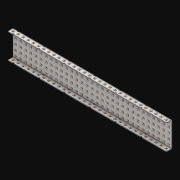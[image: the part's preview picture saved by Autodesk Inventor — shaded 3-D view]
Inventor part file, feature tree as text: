
AUTODESK INVENTOR PART (.ipt)
format: ipt  version: 2021 (Build 250183000, 183)  size: 3,827,200 bytes
history: native  units: in
note: dims shown in document units (in); Inventor stores cm internally (conversion verified against a paired STEP export)
features: extrude x218, other x217, sketch x4, thicken_offset x3, pattern_linear x3, imported_body x1
ambient origin geometry x8: Origin, YZ Plane, XZ Plane, XY Plane, X Axis, Y Axis, Z Axis, Center Point
bodies: Solid1 (feature_tree)
feature tree (446):
  thicken_offset  "Thicken1"
  thicken_offset  "Thicken2"
  thicken_offset  "Thicken3"
  pattern_linear  "Rectangular Pattern1"  Spacing1=0.001in  [1 undecoded]
  pattern_linear  "Rectangular Pattern2"  Spacing1=0.001in  [1 undecoded]
  pattern_linear  "Rectangular Pattern3"  Spacing1=0.182in  [1 undecoded]
  extrude  "Extrusion1"  Depth=0.063in TaperAngle=0.0deg
  sketch  "Sketch1"  dims[d0=0.001in]
  other  "Srf1"
  sketch  "Sketch2"  dims[d1=0.001in]
  other  "Srf2"
  sketch  "Sketch3"  dims[d2=0.001in]
  other  "Srf3"
  other  "Srf4"
  other  "Srf5"
  other  "Srf6"
  other  "Srf7"
  other  "Srf8"
  other  "Srf9"
  other  "Srf10"
  other  "Srf11"
  other  "Srf12"
  other  "Srf13"
  other  "Srf14"
  other  "Srf15"
  other  "Srf16"
  other  "Srf17"
  other  "Srf18"
  other  "Srf19"
  other  "Srf20"
  other  "Srf21"
  other  "Srf22"
  other  "Srf23"
  other  "Srf24"
  other  "Srf25"
  other  "Srf26"
  other  "Srf27"
  other  "Srf28"
  other  "Srf29"
  other  "Srf30"
  other  "Srf31"
  other  "Srf32"
  other  "Srf33"
  other  "Srf38"
  other  "Srf39"
  other  "Srf40"
  other  "Srf41"
  other  "Srf42"
  other  "Srf43"
  other  "Srf44"
  other  "Srf45"
  other  "Srf46"
  other  "Srf47"
  other  "Srf48"
  other  "Srf49"
  other  "Srf50"
  other  "Srf51"
  other  "Srf52"
  other  "Srf53"
  other  "Srf54"
  other  "Srf55"
  other  "Srf56"
  other  "Srf57"
  other  "Srf58"
  other  "Srf59"
  other  "Srf60"
  other  "Srf61"
  other  "Srf62"
  other  "Srf63"
  other  "Srf64"
  other  "Srf65"
  other  "Srf66"
  other  "Srf67"
  other  "Srf72"
  other  "Srf73"
  other  "Srf74"
  other  "Srf75"
  other  "Srf76"
  other  "Srf77"
  other  "Srf78"
  other  "Srf79"
  other  "Srf80"
  other  "Srf81"
  other  "Srf82"
  other  "Srf83"
  other  "Srf84"
  other  "Srf85"
  other  "Srf86"
  other  "Srf87"
  other  "Srf88"
  other  "Srf89"
  other  "Srf90"
  other  "Srf91"
  other  "Srf92"
  other  "Srf93"
  other  "Srf94"
  other  "Srf95"
  other  "Srf96"
  other  "Srf97"
  other  "Srf98"
  other  "Srf99"
  other  "Srf100"
  other  "Srf101"
  other  "Srf106"
  other  "Srf107"
  other  "Srf108"
  other  "Srf109"
  other  "Srf110"
  other  "Srf111"
  other  "Srf112"
  other  "Srf113"
  other  "Srf114"
  other  "Srf115"
  other  "Srf116"
  other  "Srf117"
  other  "Srf118"
  other  "Srf119"
  other  "Srf120"
  other  "Srf121"
  other  "Srf122"
  other  "Srf123"
  other  "Srf124"
  other  "Srf125"
  other  "Srf126"
  other  "Srf127"
  other  "Srf128"
  other  "Srf129"
  other  "Srf130"
  other  "Srf131"
  other  "Srf132"
  other  "Srf133"
  other  "Srf134"
  other  "Srf135"
  other  "Srf136"
  other  "Srf141"
  other  "Srf142"
  other  "Srf143"
  other  "Srf144"
  other  "Srf145"
  other  "Srf146"
  other  "Srf147"
  other  "Srf148"
  other  "Srf149"
  other  "Srf150"
  other  "Srf151"
  other  "Srf152"
  other  "Srf153"
  other  "Srf154"
  other  "Srf155"
  other  "Srf156"
  other  "Srf157"
  other  "Srf158"
  other  "Srf159"
  other  "Srf160"
  other  "Srf161"
  other  "Srf162"
  other  "Srf163"
  other  "Srf164"
  other  "Srf165"
  other  "Srf166"
  other  "Srf167"
  other  "Srf168"
  other  "Srf169"
  other  "Srf170"
  other  "Srf171"
  other  "Srf176"
  other  "Srf177"
  other  "Srf178"
  other  "Srf179"
  other  "Srf180"
  other  "Srf181"
  other  "Srf182"
  other  "Srf183"
  other  "Srf184"
  other  "Srf185"
  other  "Srf186"
  other  "Srf187"
  other  "Srf188"
  other  "Srf189"
  other  "Srf190"
  other  "Srf191"
  other  "Srf192"
  other  "Srf193"
  other  "Srf194"
  other  "Srf195"
  other  "Srf196"
  other  "Srf197"
  other  "Srf198"
  other  "Srf199"
  other  "Srf200"
  other  "Srf201"
  other  "Srf202"
  other  "Srf203"
  other  "Srf204"
  other  "Srf205"
  other  "Srf206"
  other  "Srf211"
  other  "Srf212"
  other  "Srf213"
  other  "Srf214"
  other  "Srf215"
  other  "Srf216"
  other  "Srf217"
  other  "Srf218"
  other  "Srf219"
  other  "Srf220"
  other  "Srf221"
  other  "Srf222"
  other  "Srf223"
  other  "Srf224"
  other  "Srf225"
  other  "Srf226"
  other  "Srf227"
  other  "Srf228"
  other  "Srf229"
  other  "Srf230"
  other  "Srf231"
  other  "Srf232"
  other  "Srf233"
  other  "Srf234"
  other  "Srf235"
  other  "Srf236"
  other  "Srf237"
  other  "Srf238"
  other  "Srf239"
  other  "Srf240"
  other  "Srf241"
  sketch  "Sketch4"  dims[d3=0.001in d4=0.001in d5=0.001in d6=0.182in d7=0.063in d8=0.0in d9=0.182in d10=0.063in d11=0.0in d12=0.182in d13=0.063in d14=0.0in d17=0.5in d18=12.2047in d20=0.5in d21=12.2047in d23=0.5in d24=1.9685in d26=0.5in d27=2.0in d28=0.0in]
  imported_body  "Imported1"
  extrude  "ExtrusionSrf1"  Depth=2.0in
  extrude  "ExtrusionSrf2"  Depth=0.063in TaperAngle=0.0deg
  extrude  "ExtrusionSrf3"  Depth=2.0in
  extrude  "ExtrusionSrf4"  Depth=0.063in TaperAngle=0.0deg
  extrude  "ExtrusionSrf5"  Depth=0.5in
  extrude  "ExtrusionSrf6"  Depth=2.0in
  extrude  "ExtrusionSrf7"  Depth=0.5in
  extrude  "ExtrusionSrf8"  Depth=2.0in
  extrude  "ExtrusionSrf9"  Depth=0.5in
  extrude  "ExtrusionSrf10"  Depth=0.5in
  extrude  "ExtrusionSrf11"  Depth=2.0in
  extrude  "ExtrusionSrf12"  TaperAngle=0.0deg  [1 undecoded]
  extrude  "ExtrusionSrf13"  [1 undecoded]
  extrude  "ExtrusionSrf14"  [1 undecoded]
  extrude  "ExtrusionSrf15"  [1 undecoded]
  extrude  "ExtrusionSrf16"  [1 undecoded]
  extrude  "ExtrusionSrf17"  [1 undecoded]
  extrude  "ExtrusionSrf18"  [1 undecoded]
  extrude  "ExtrusionSrf19"  [1 undecoded]
  extrude  "ExtrusionSrf20"  [1 undecoded]
  extrude  "ExtrusionSrf21"  [1 undecoded]
  extrude  "ExtrusionSrf22"  [1 undecoded]
  extrude  "ExtrusionSrf23"  [1 undecoded]
  extrude  "ExtrusionSrf24"  [1 undecoded]
  extrude  "ExtrusionSrf25"  [1 undecoded]
  extrude  "ExtrusionSrf26"  [1 undecoded]
  extrude  "ExtrusionSrf27"  [1 undecoded]
  extrude  "ExtrusionSrf28"  [1 undecoded]
  extrude  "ExtrusionSrf29"  [1 undecoded]
  extrude  "ExtrusionSrf30"  [1 undecoded]
  extrude  "ExtrusionSrf31"  [1 undecoded]
  extrude  "ExtrusionSrf32"  [1 undecoded]
  extrude  "ExtrusionSrf33"  [1 undecoded]
  extrude  "ExtrusionSrf38"  [1 undecoded]
  extrude  "ExtrusionSrf39"  [1 undecoded]
  extrude  "ExtrusionSrf40"  [1 undecoded]
  extrude  "ExtrusionSrf41"  [1 undecoded]
  extrude  "ExtrusionSrf42"  [1 undecoded]
  extrude  "ExtrusionSrf43"  [1 undecoded]
  extrude  "ExtrusionSrf44"  [1 undecoded]
  extrude  "ExtrusionSrf45"  [1 undecoded]
  extrude  "ExtrusionSrf46"  [1 undecoded]
  extrude  "ExtrusionSrf47"  [1 undecoded]
  extrude  "ExtrusionSrf48"  [1 undecoded]
  extrude  "ExtrusionSrf49"  [1 undecoded]
  extrude  "ExtrusionSrf50"  [1 undecoded]
  extrude  "ExtrusionSrf51"  [1 undecoded]
  extrude  "ExtrusionSrf52"  [1 undecoded]
  extrude  "ExtrusionSrf53"  [1 undecoded]
  extrude  "ExtrusionSrf54"  [1 undecoded]
  extrude  "ExtrusionSrf55"  [1 undecoded]
  extrude  "ExtrusionSrf56"  [1 undecoded]
  extrude  "ExtrusionSrf57"  [1 undecoded]
  extrude  "ExtrusionSrf58"  [1 undecoded]
  extrude  "ExtrusionSrf59"  [1 undecoded]
  extrude  "ExtrusionSrf60"  [1 undecoded]
  extrude  "ExtrusionSrf61"  [1 undecoded]
  extrude  "ExtrusionSrf62"  [1 undecoded]
  extrude  "ExtrusionSrf63"  [1 undecoded]
  extrude  "ExtrusionSrf64"  [1 undecoded]
  extrude  "ExtrusionSrf65"  [1 undecoded]
  extrude  "ExtrusionSrf66"  [1 undecoded]
  extrude  "ExtrusionSrf67"  [1 undecoded]
  extrude  "ExtrusionSrf72"  [1 undecoded]
  extrude  "ExtrusionSrf73"  [1 undecoded]
  extrude  "ExtrusionSrf74"  [1 undecoded]
  extrude  "ExtrusionSrf75"  [1 undecoded]
  extrude  "ExtrusionSrf76"  [1 undecoded]
  extrude  "ExtrusionSrf77"  [1 undecoded]
  extrude  "ExtrusionSrf78"  [1 undecoded]
  extrude  "ExtrusionSrf79"  [1 undecoded]
  extrude  "ExtrusionSrf80"  [1 undecoded]
  extrude  "ExtrusionSrf81"  [1 undecoded]
  extrude  "ExtrusionSrf82"  [1 undecoded]
  extrude  "ExtrusionSrf83"  [1 undecoded]
  extrude  "ExtrusionSrf84"  [1 undecoded]
  extrude  "ExtrusionSrf85"  [1 undecoded]
  extrude  "ExtrusionSrf86"  [1 undecoded]
  extrude  "ExtrusionSrf87"  [1 undecoded]
  extrude  "ExtrusionSrf88"  [1 undecoded]
  extrude  "ExtrusionSrf89"  [1 undecoded]
  extrude  "ExtrusionSrf90"  [1 undecoded]
  extrude  "ExtrusionSrf91"  [1 undecoded]
  extrude  "ExtrusionSrf92"  [1 undecoded]
  extrude  "ExtrusionSrf93"  [1 undecoded]
  extrude  "ExtrusionSrf94"  [1 undecoded]
  extrude  "ExtrusionSrf95"  [1 undecoded]
  extrude  "ExtrusionSrf96"  [1 undecoded]
  extrude  "ExtrusionSrf97"  [1 undecoded]
  extrude  "ExtrusionSrf98"  [1 undecoded]
  extrude  "ExtrusionSrf99"  [1 undecoded]
  extrude  "ExtrusionSrf100"  [1 undecoded]
  extrude  "ExtrusionSrf101"  [1 undecoded]
  extrude  "ExtrusionSrf106"  [1 undecoded]
  extrude  "ExtrusionSrf107"  [1 undecoded]
  extrude  "ExtrusionSrf108"  [1 undecoded]
  extrude  "ExtrusionSrf109"  [1 undecoded]
  extrude  "ExtrusionSrf110"  [1 undecoded]
  extrude  "ExtrusionSrf111"  [1 undecoded]
  extrude  "ExtrusionSrf112"  [1 undecoded]
  extrude  "ExtrusionSrf113"  [1 undecoded]
  extrude  "ExtrusionSrf114"  [1 undecoded]
  extrude  "ExtrusionSrf115"  [1 undecoded]
  extrude  "ExtrusionSrf116"  [1 undecoded]
  extrude  "ExtrusionSrf117"  [1 undecoded]
  extrude  "ExtrusionSrf118"  [1 undecoded]
  extrude  "ExtrusionSrf119"  [1 undecoded]
  extrude  "ExtrusionSrf120"  [1 undecoded]
  extrude  "ExtrusionSrf121"  [1 undecoded]
  extrude  "ExtrusionSrf122"  [1 undecoded]
  extrude  "ExtrusionSrf123"  [1 undecoded]
  extrude  "ExtrusionSrf124"  [1 undecoded]
  extrude  "ExtrusionSrf125"  [1 undecoded]
  extrude  "ExtrusionSrf126"  [1 undecoded]
  extrude  "ExtrusionSrf127"  [1 undecoded]
  extrude  "ExtrusionSrf128"  [1 undecoded]
  extrude  "ExtrusionSrf129"  [1 undecoded]
  extrude  "ExtrusionSrf130"  [1 undecoded]
  extrude  "ExtrusionSrf131"  [1 undecoded]
  extrude  "ExtrusionSrf132"  [1 undecoded]
  extrude  "ExtrusionSrf133"  [1 undecoded]
  extrude  "ExtrusionSrf134"  [1 undecoded]
  extrude  "ExtrusionSrf135"  [1 undecoded]
  extrude  "ExtrusionSrf136"  [1 undecoded]
  extrude  "ExtrusionSrf141"  [1 undecoded]
  extrude  "ExtrusionSrf142"  [1 undecoded]
  extrude  "ExtrusionSrf143"  [1 undecoded]
  extrude  "ExtrusionSrf144"  [1 undecoded]
  extrude  "ExtrusionSrf145"  [1 undecoded]
  extrude  "ExtrusionSrf146"  [1 undecoded]
  extrude  "ExtrusionSrf147"  [1 undecoded]
  extrude  "ExtrusionSrf148"  [1 undecoded]
  extrude  "ExtrusionSrf149"  [1 undecoded]
  extrude  "ExtrusionSrf150"  [1 undecoded]
  extrude  "ExtrusionSrf151"  [1 undecoded]
  extrude  "ExtrusionSrf152"  [1 undecoded]
  extrude  "ExtrusionSrf153"  [1 undecoded]
  extrude  "ExtrusionSrf154"  [1 undecoded]
  extrude  "ExtrusionSrf155"  [1 undecoded]
  extrude  "ExtrusionSrf156"  [1 undecoded]
  extrude  "ExtrusionSrf157"  [1 undecoded]
  extrude  "ExtrusionSrf158"  [1 undecoded]
  extrude  "ExtrusionSrf159"  [1 undecoded]
  extrude  "ExtrusionSrf160"  [1 undecoded]
  extrude  "ExtrusionSrf161"  [1 undecoded]
  extrude  "ExtrusionSrf162"  [1 undecoded]
  extrude  "ExtrusionSrf163"  [1 undecoded]
  extrude  "ExtrusionSrf164"  [1 undecoded]
  extrude  "ExtrusionSrf165"  [1 undecoded]
  extrude  "ExtrusionSrf166"  [1 undecoded]
  extrude  "ExtrusionSrf167"  [1 undecoded]
  extrude  "ExtrusionSrf168"  [1 undecoded]
  extrude  "ExtrusionSrf169"  [1 undecoded]
  extrude  "ExtrusionSrf170"  [1 undecoded]
  extrude  "ExtrusionSrf171"  [1 undecoded]
  extrude  "ExtrusionSrf176"  [1 undecoded]
  extrude  "ExtrusionSrf177"  [1 undecoded]
  extrude  "ExtrusionSrf178"  [1 undecoded]
  extrude  "ExtrusionSrf179"  [1 undecoded]
  extrude  "ExtrusionSrf180"  [1 undecoded]
  extrude  "ExtrusionSrf181"  [1 undecoded]
  extrude  "ExtrusionSrf182"  [1 undecoded]
  extrude  "ExtrusionSrf183"  [1 undecoded]
  extrude  "ExtrusionSrf184"  [1 undecoded]
  extrude  "ExtrusionSrf185"  [1 undecoded]
  extrude  "ExtrusionSrf186"  [1 undecoded]
  extrude  "ExtrusionSrf187"  [1 undecoded]
  extrude  "ExtrusionSrf188"  [1 undecoded]
  extrude  "ExtrusionSrf189"  [1 undecoded]
  extrude  "ExtrusionSrf190"  [1 undecoded]
  extrude  "ExtrusionSrf191"  [1 undecoded]
  extrude  "ExtrusionSrf192"  [1 undecoded]
  extrude  "ExtrusionSrf193"  [1 undecoded]
  extrude  "ExtrusionSrf194"  [1 undecoded]
  extrude  "ExtrusionSrf195"  [1 undecoded]
  extrude  "ExtrusionSrf196"  [1 undecoded]
  extrude  "ExtrusionSrf197"  [1 undecoded]
  extrude  "ExtrusionSrf198"  [1 undecoded]
  extrude  "ExtrusionSrf199"  [1 undecoded]
  extrude  "ExtrusionSrf200"  [1 undecoded]
  extrude  "ExtrusionSrf201"  [1 undecoded]
  extrude  "ExtrusionSrf202"  [1 undecoded]
  extrude  "ExtrusionSrf203"  [1 undecoded]
  extrude  "ExtrusionSrf204"  [1 undecoded]
  extrude  "ExtrusionSrf205"  [1 undecoded]
  extrude  "ExtrusionSrf206"  [1 undecoded]
  extrude  "ExtrusionSrf211"  [1 undecoded]
  extrude  "ExtrusionSrf212"  [1 undecoded]
  extrude  "ExtrusionSrf213"  [1 undecoded]
  extrude  "ExtrusionSrf214"  [1 undecoded]
  extrude  "ExtrusionSrf215"  [1 undecoded]
  extrude  "ExtrusionSrf216"  [1 undecoded]
  extrude  "ExtrusionSrf217"  [1 undecoded]
  extrude  "ExtrusionSrf218"  [1 undecoded]
  extrude  "ExtrusionSrf219"  [1 undecoded]
  extrude  "ExtrusionSrf220"  [1 undecoded]
  extrude  "ExtrusionSrf221"  [1 undecoded]
  extrude  "ExtrusionSrf222"  [1 undecoded]
  extrude  "ExtrusionSrf223"  [1 undecoded]
  extrude  "ExtrusionSrf224"  [1 undecoded]
  extrude  "ExtrusionSrf225"  [1 undecoded]
  extrude  "ExtrusionSrf226"  [1 undecoded]
  extrude  "ExtrusionSrf227"  [1 undecoded]
  extrude  "ExtrusionSrf228"  [1 undecoded]
  extrude  "ExtrusionSrf229"  [1 undecoded]
  extrude  "ExtrusionSrf230"  [1 undecoded]
  extrude  "ExtrusionSrf231"  [1 undecoded]
  extrude  "ExtrusionSrf232"  [1 undecoded]
  extrude  "ExtrusionSrf233"  [1 undecoded]
  extrude  "ExtrusionSrf234"  [1 undecoded]
  extrude  "ExtrusionSrf235"  [1 undecoded]
  extrude  "ExtrusionSrf236"  [1 undecoded]
  extrude  "ExtrusionSrf237"  [1 undecoded]
  extrude  "ExtrusionSrf238"  [1 undecoded]
  extrude  "ExtrusionSrf239"  [1 undecoded]
  extrude  "ExtrusionSrf240"  [1 undecoded]
  extrude  "ExtrusionSrf241"  [1 undecoded]
note: 209 required parameter values undecoded (feature->parameter linkage not recoverable at this tier; creation-order binding heuristic only, values carry confidence <= 0.55)
